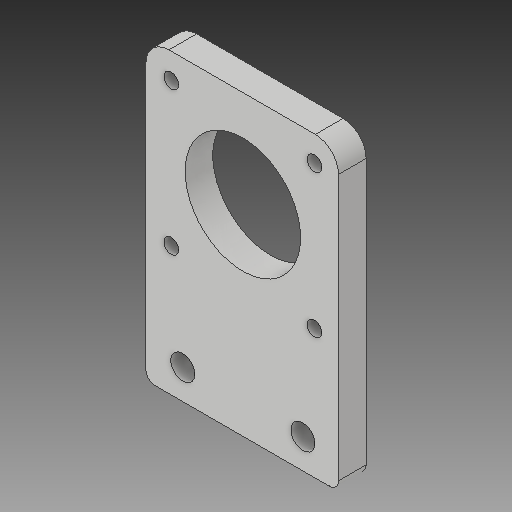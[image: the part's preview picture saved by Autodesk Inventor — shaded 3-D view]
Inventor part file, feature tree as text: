
AUTODESK INVENTOR PART (.ipt)
format: ipt  version: 2017 (Build 210142000, 142)  size: 144,896 bytes
history: native  units: mm
features: sketch x4, other x3
ambient origin geometry x8: Origin, YZ Plane, XZ Plane, XY Plane, X Axis, Y Axis, Z Axis, Center Point
bodies: Solid1 (feature_tree)
feature tree (7):
  other  "Z Motor Mount LC.ipt"
  other  "Solid1::Z Motor Mount LC.ipt"
  other  "TaggingFeature1"
  sketch  "Sketch1"  dims[d0=10.0mm]
  sketch  "Sketch2"
  sketch  "Sketch3"
  sketch  "Sketch4"
